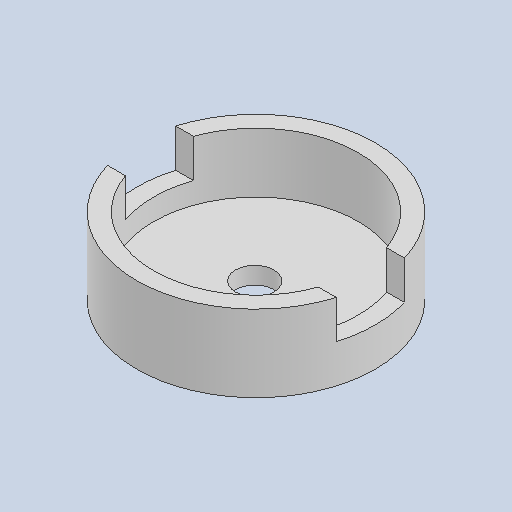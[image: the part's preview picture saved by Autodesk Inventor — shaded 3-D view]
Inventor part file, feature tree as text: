
AUTODESK INVENTOR PART (.ipt)
format: ipt  version: 2022.1 (Build 261234020, 234B)  size: 125,440 bytes
history: native  units: mm
features: sketch x4, extrude x4, hole x1
ambient origin geometry x8: Origin, YZ Plane, XZ Plane, XY Plane, X Axis, Y Axis, Z Axis, Center Point
bodies: Solid1 (feature_tree)
feature tree (9):
  sketch  "Sketch1"  dims[d0=28.0mm d1=24.0mm]
  extrude  "Extrusion1"  Depth=24.0mm
  extrude  "Extrusion2"  Depth=7.0mm
  extrude  "Extrusion3"  Depth=8.0mm TaperAngle=0.0deg
  hole  "Hole2"  [1 undecoded]
  extrude  "Extrusion4"  Depth=2.5mm TaperAngle=0.0deg
  sketch  "Sketch2"  dims[d2=7.0mm d3=0.0mm d4=28.0mm]
  sketch  "Sketch3"  dims[d5=8.0mm d6=8.0mm d7=0.0mm]
  sketch  "Sketch5"  dims[d8=2.0mm d9=0.0mm d17=28.0mm d18=4.5mm d19=6.0mm d20=10.59mm d21=3.0mm d22=90.0deg d23=8.0mm d24=20.594885mm d25=2.5mm d26=0.0mm]
note: 1 required parameter value undecoded (feature->parameter linkage not recoverable at this tier; creation-order binding heuristic only, values carry confidence <= 0.55)
